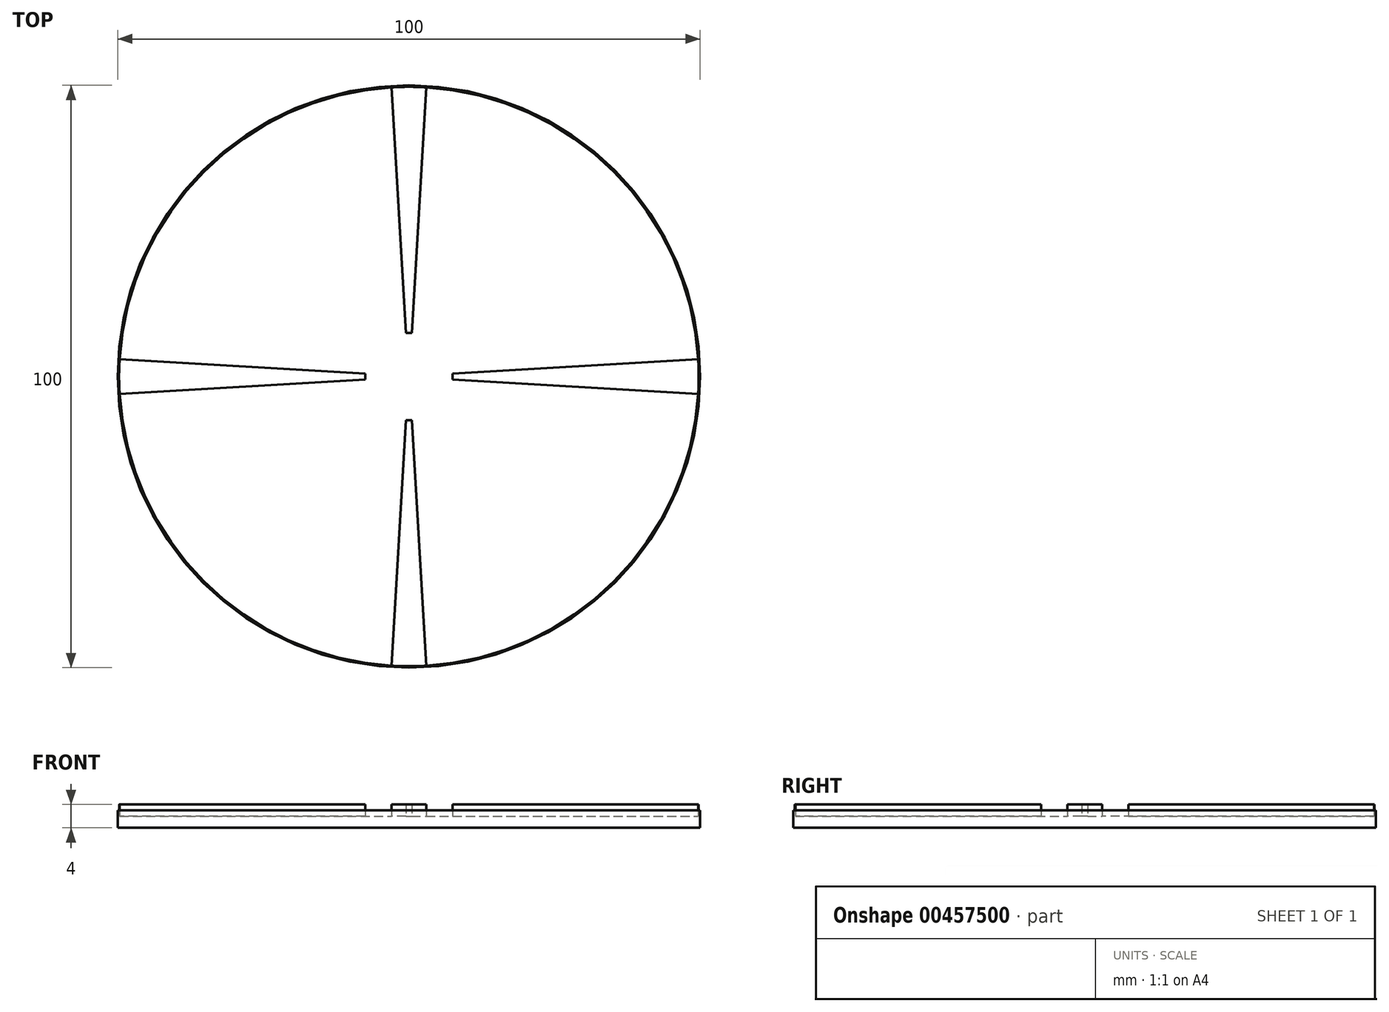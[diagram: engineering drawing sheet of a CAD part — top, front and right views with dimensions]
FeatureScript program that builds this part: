
annotation { "Feature Type Name" : "Feature", "Feature Type Description" : "" }
export const myFeature = defineFeature(function(context is Context, id is Id, definition is map)
    precondition{}
    {
        {
            var Q0;
            Q0=qCreatedBy(makeId("Top.planeOp"),FACE);
            var sketch = newSketch(context, id + "F0", { "sketchPlane" : qUnion([Q0])});
            skLineSegment(sketch, "E0.bottom", {"start": v(75, 70) * mm, "end": v(-75, 70) * mm});
            skLineSegment(sketch, "E0.top", {"start": v(75, -70) * mm, "end": v(-75, -70) * mm});
            skLineSegment(sketch, "E0.left", {"start": v(75, 70) * mm, "end": v(75, -70) * mm});
            skLineSegment(sketch, "E0.right", {"start": v(-75, 70) * mm, "end": v(-75, -70) * mm});
            skPoint(sketch, "E0.middle", {"position": v(0, 0) * mm});
            skSolve(sketch);
        }
        {
            var Q0;
            Q0=qSketchRegion(id+"F0",true);
            extrude(context, id + "F1", {"entities" : qUnion([Q0]), "depth" : 2 * mm});
        }
        {
            var Q0;
            Q0=makeQuery(id+"F1.opExtrude","CAP_FACE",FACE,{"disambiguationData":[OSD([sQuery(id+"F0.wireOp",EDGE,"E0.bottom"),sQuery(id+"F0.wireOp",EDGE,"E0.top"),sQuery(id+"F0.wireOp",EDGE,"E0.left"),sQuery(id+"F0.wireOp",EDGE,"E0.right")])],"isStart":false});
            var sketch = newSketch(context, id + "F2", { "sketchPlane" : qUnion([Q0])});
            skArc(sketch, "E1", {"start": v(-67.18, 7) * mm, "mid": v(-67.92, 8.77) * mm, "end": v(-69.68, 9.5) * mm});
            skArc(sketch, "E2.MirrorC", {"start": v(-67.18, -7) * mm, "mid": v(-67.92, -8.77) * mm, "end": v(-69.68, -9.5) * mm});
            skCircle(sketch, "E3", {"center": v(-64, 57.6) * mm, "radius": 2.5 * mm});
            skCircle(sketch, "E4.MirrorC", {"center": v(-64, -57.6) * mm, "radius": 2.5 * mm});
            skLineSegment(sketch, "E5", {"start": v(-46.5, 70) * mm, "end": v(-75, 41.5) * mm});
            skLineSegment(sketch, "E6.MirrorCS", {"start": v(-46.5, -70) * mm, "end": v(-75, -41.5) * mm});
            skLineSegment(sketch, "E7", {"start": v(-69.68, 9.5) * mm, "end": v(-75, 9.5) * mm});
            skLineSegment(sketch, "E8", {"start": v(-67.18, -7) * mm, "end": v(-67.18, 7) * mm});
            skLineSegment(sketch, "E9.MirrorCS", {"start": v(-69.68, -9.5) * mm, "end": v(-75, -9.5) * mm});
            skLineSegment(sketch, "E10", {"start": v(-15, -70) * mm, "end": v(-16.5, -66.52) * mm});
            skArc(sketch, "E11", {"start": v(-16.5, -66.52) * mm, "mid": v(-21.54, -63.23) * mm, "end": v(-26.53, -66.6) * mm});
            skLineSegment(sketch, "E12", {"start": v(-26.53, -66.6) * mm, "end": v(-27.94, -70) * mm});
            skLineSegment(sketch, "E13", {"start": v(-27.95, 70) * mm, "end": v(-26.64, 66.44) * mm});
            skLineSegment(sketch, "E14", {"start": v(-15, 70) * mm, "end": v(-16.65, 66.59) * mm});
            skArc(sketch, "E15", {"start": v(-26.64, 66.44) * mm, "mid": v(-21.6, 63.23) * mm, "end": v(-16.65, 66.59) * mm});
            skSolve(sketch);
        }
        {
            var Q0;
            Q0 = qSketchRegion(id + "F2", true);
            var Q1;
            Q1=makeQuery(id+"F2.imprint","IMPRINT",FACE,{"disambiguationData":[TD([[makeQuery(id+"F2.imprint","IMPRINT",EDGE,{"derivedFrom":sQuery(id+"F2.wireOp",EDGE,"E3")}),-1.0]])]});
            var Q2;
            {var subQ0=sQuery(id+"F2.wireOp",EDGE,"E13");Q2=makeQuery(id+"F2.imprint","IMPRINT",FACE,{"disambiguationData":[TD([[makeQuery(id+"F2.imprint","IMPRINT",EDGE,{"derivedFrom":subQ0}),1.0]])]});}
            var Q3;
            Q3=makeQuery(id+"F2.imprint","IMPRINT",FACE,{"disambiguationData":[TD([[makeQuery(id+"F2.imprint","IMPRINT",EDGE,{"derivedFrom":sQuery(id+"F2.wireOp",EDGE,"E1")}),1.0]])]});
            var Q4;
            {var subQ0=sQuery(id+"F2.wireOp",EDGE,"E10");Q4=makeQuery(id+"F2.imprint","IMPRINT",FACE,{"disambiguationData":[TD([[makeQuery(id+"F2.imprint","IMPRINT",EDGE,{"derivedFrom":subQ0}),1.0]])]});}
            var Q5;
            Q5=makeQuery(id+"F2.imprint","IMPRINT",FACE,{"disambiguationData":[TD([[makeQuery(id+"F2.imprint","IMPRINT",EDGE,{"derivedFrom":sQuery(id+"F2.wireOp",EDGE,"E4.MirrorC")}),1.0]])]});
            extrude(context, id + "F3", {"entities" : qUnion([Q0, Q1, Q2, Q3, Q4, Q5]), "operationType" : NewBodyOperationType.REMOVE, "endBound" : BoundingType.THROUGH_ALL, "oppositeDirection" : true, "depth" : 5 * mm, "offsetDistance" : 25 * mm});
        }
        {
            var Q0;
            Q0=makeQuery(id+"F1.opExtrude","CAP_FACE",FACE,{"disambiguationData":[OSD([sQuery(id+"F0.wireOp",EDGE,"E0.bottom"),sQuery(id+"F0.wireOp",EDGE,"E0.top"),sQuery(id+"F0.wireOp",EDGE,"E0.left"),sQuery(id+"F0.wireOp",EDGE,"E0.right")])],"isStart":false});
            var sketch = newSketch(context, id + "F4", { "sketchPlane" : qUnion([Q0])});
            skCircle(sketch, "E16", {"center": v(-3.16, 0) * mm, "radius": 49.75 * mm});
            skCircle(sketch, "E17", {"center": v(-3.16, 0) * mm, "radius": 50 * mm});
            skSolve(sketch);
        }
        {
            var Q0;
            Q0=makeQuery(id+"F4.imprint","IMPRINT",FACE,{"disambiguationData":[TD([[makeQuery(id+"F4.imprint","IMPRINT",EDGE,{"derivedFrom":sQuery(id+"F4.wireOp",EDGE,"E16")}),-1.0]])]});
            extrude(context, id + "F5", {"entities" : qUnion([Q0]), "operationType" : NewBodyOperationType.ADD, "depth" : 1 * mm});
        }
        {
            var Q0;
            Q0=makeQuery(id+"F5.boolean.opBoolean","SPLIT",FACE,{"disambiguationData":[TD([makeQuery(id+"F5.opExtrude","SWEPT_FACE",FACE,{"disambiguationData":[OSD([sQuery(id+"F4.wireOp",EDGE,"E16")])]})])],"derivedFrom":makeQuery(id+"F1.opExtrude","CAP_FACE",FACE,{"disambiguationData":[OSD([sQuery(id+"F0.wireOp",EDGE,"E0.bottom"),sQuery(id+"F0.wireOp",EDGE,"E0.top"),sQuery(id+"F0.wireOp",EDGE,"E0.left"),sQuery(id+"F0.wireOp",EDGE,"E0.right")])],"isStart":false})});
            var sketch = newSketch(context, id + "F6", { "sketchPlane" : qUnion([Q0])});
            skLineSegment(sketch, "E18", {"start": v(-52.91, 0) * mm, "end": v(46.59, 0) * mm});
            skLineSegment(sketch, "E19", {"start": v(-3.16, -49.75) * mm, "end": v(-3.16, 49.75) * mm});
            skPoint(sketch, "E20.center", {"position": v(-3.16, 0) * mm});
            skPoint(sketch, "E21", {"position": v(-3.16, 7.5) * mm});
            skPoint(sketch, "E22.1.0", {"position": v(-10.66, 0) * mm});
            skPoint(sketch, "E22.2.0", {"position": v(-3.16, -7.5) * mm});
            skPoint(sketch, "E22.3.0", {"position": v(4.34, 0) * mm});
            skLineSegment(sketch, "E23", {"start": v(-3.16, 7.5) * mm, "end": v(-3.66, 7.5) * mm});
            skLineSegment(sketch, "E24", {"start": v(-3.66, 7.5) * mm, "end": v(-6.16, 49.66) * mm});
            skLineSegment(sketch, "E25.MirrorCS", {"start": v(-2.66, 7.5) * mm, "end": v(-0.16, 49.66) * mm});
            skLineSegment(sketch, "E26.MirrorCS", {"start": v(-3.16, 7.5) * mm, "end": v(-2.66, 7.5) * mm});
            skLineSegment(sketch, "E27.1.0", {"start": v(-10.66, -0.5) * mm, "end": v(-52.82, -3) * mm});
            skLineSegment(sketch, "E27.1.1", {"start": v(-10.66, 0.5) * mm, "end": v(-52.82, 3) * mm});
            skLineSegment(sketch, "E27.1.2", {"start": v(-10.66, 0) * mm, "end": v(-10.66, 0.5) * mm});
            skLineSegment(sketch, "E27.1.3", {"start": v(-10.66, 0) * mm, "end": v(-10.66, -0.5) * mm});
            skLineSegment(sketch, "E27.2.0", {"start": v(-2.66, -7.5) * mm, "end": v(-0.16, -49.66) * mm});
            skLineSegment(sketch, "E27.2.1", {"start": v(-3.66, -7.5) * mm, "end": v(-6.16, -49.66) * mm});
            skLineSegment(sketch, "E27.2.2", {"start": v(-3.16, -7.5) * mm, "end": v(-3.66, -7.5) * mm});
            skLineSegment(sketch, "E27.2.3", {"start": v(-3.16, -7.5) * mm, "end": v(-2.66, -7.5) * mm});
            skLineSegment(sketch, "E27.3.0", {"start": v(4.34, 0.5) * mm, "end": v(46.5, 3) * mm});
            skLineSegment(sketch, "E27.3.1", {"start": v(4.34, -0.5) * mm, "end": v(46.5, -3) * mm});
            skLineSegment(sketch, "E27.3.2", {"start": v(4.34, 0) * mm, "end": v(4.34, -0.5) * mm});
            skLineSegment(sketch, "E27.3.3", {"start": v(4.34, 0) * mm, "end": v(4.34, 0.5) * mm});
            skSolve(sketch);
        }
        {
            var Q0;
            {var subQ4=sQuery(id+"F6.wireOp",EDGE,"E25.MirrorCS");Q0=makeQuery(id+"F6.imprint","IMPRINT",FACE,{"disambiguationData":[TD([[makeQuery(id+"F6.imprint","IMPRINT",EDGE,{"derivedFrom":subQ4}),1.0]])]});}
            var Q1;
            Q1=makeQuery(id+"F6.imprint","IMPRINT",FACE,{"disambiguationData":[TD([[makeQuery(id+"F6.imprint","IMPRINT",EDGE,{"derivedFrom":sQuery(id+"F6.wireOp",EDGE,"NAewh5kq-L7EF-FmbW-yRkp-duXd5l4xCfDB")}),-1.0]])]});
            var Q2;
            Q2=makeQuery(id+"F6.imprint","IMPRINT",FACE,{"disambiguationData":[TD([[makeQuery(id+"F6.imprint","IMPRINT",EDGE,{"derivedFrom":sQuery(id+"F6.wireOp",EDGE,"c465f5bf-b5a5-4b0b-8659-c38a877ec2590.MirrorC")}),1.0]])]});
            var Q3;
            {var subQ4=sQuery(id+"F6.wireOp",EDGE,"E27.3.1");Q3=makeQuery(id+"F6.imprint","IMPRINT",FACE,{"disambiguationData":[TD([[makeQuery(id+"F6.imprint","IMPRINT",EDGE,{"derivedFrom":subQ4}),1.0]])]});}
            var Q4;
            Q4=makeQuery(id+"F6.imprint","IMPRINT",FACE,{"disambiguationData":[TD([[makeQuery(id+"F6.imprint","IMPRINT",EDGE,{"derivedFrom":sQuery(id+"F6.wireOp",EDGE,"E20.3.0")}),1.0]])]});
            var Q5;
            Q5=makeQuery(id+"F6.imprint","IMPRINT",FACE,{"disambiguationData":[TD([[makeQuery(id+"F6.imprint","IMPRINT",EDGE,{"derivedFrom":sQuery(id+"F6.wireOp",EDGE,"E20.1.0")}),1.0]])]});
            var Q6;
            {var subQ4=sQuery(id+"F6.wireOp",EDGE,"E27.1.1");Q6=makeQuery(id+"F6.imprint","IMPRINT",FACE,{"disambiguationData":[TD([[makeQuery(id+"F6.imprint","IMPRINT",EDGE,{"derivedFrom":subQ4}),1.0]])]});}
            var Q7;
            {var subQ4=sQuery(id+"F6.wireOp",EDGE,"E27.2.1");Q7=makeQuery(id+"F6.imprint","IMPRINT",FACE,{"disambiguationData":[TD([[makeQuery(id+"F6.imprint","IMPRINT",EDGE,{"derivedFrom":subQ4}),1.0]])]});}
            var Q8;
            Q8=makeQuery(id+"F6.imprint","IMPRINT",FACE,{"disambiguationData":[TD([[makeQuery(id+"F6.imprint","IMPRINT",EDGE,{"derivedFrom":sQuery(id+"F6.wireOp",EDGE,"E20.2.0")}),1.0]])]});
            var Q9;
            {var subQ4=sQuery(id+"F6.wireOp",EDGE,"E27.3.0");Q9=makeQuery(id+"F6.imprint","IMPRINT",FACE,{"disambiguationData":[TD([[makeQuery(id+"F6.imprint","IMPRINT",EDGE,{"derivedFrom":subQ4}),-1.0]])]});}
            var Q10;
            Q10=makeQuery(id+"F6.imprint","IMPRINT",FACE,{"disambiguationData":[TD([[makeQuery(id+"F6.imprint","IMPRINT",EDGE,{"derivedFrom":sQuery(id+"F6.wireOp",EDGE,"E20.3.1")}),-1.0]])]});
            var Q11;
            Q11=makeQuery(id+"F6.imprint","IMPRINT",FACE,{"disambiguationData":[TD([[makeQuery(id+"F6.imprint","IMPRINT",EDGE,{"derivedFrom":sQuery(id+"F6.wireOp",EDGE,"E20.1.1")}),-1.0]])]});
            var Q12;
            {var subQ4=sQuery(id+"F6.wireOp",EDGE,"E27.1.0");Q12=makeQuery(id+"F6.imprint","IMPRINT",FACE,{"disambiguationData":[TD([[makeQuery(id+"F6.imprint","IMPRINT",EDGE,{"derivedFrom":subQ4}),-1.0]])]});}
            var Q13;
            Q13=makeQuery(id+"F6.imprint","IMPRINT",FACE,{"disambiguationData":[TD([[makeQuery(id+"F6.imprint","IMPRINT",EDGE,{"derivedFrom":sQuery(id+"F6.wireOp",EDGE,"E20.2.1")}),-1.0]])]});
            var Q14;
            {var subQ4=sQuery(id+"F6.wireOp",EDGE,"E27.2.0");Q14=makeQuery(id+"F6.imprint","IMPRINT",FACE,{"disambiguationData":[TD([[makeQuery(id+"F6.imprint","IMPRINT",EDGE,{"derivedFrom":subQ4}),-1.0]])]});}
            var Q15;
            {var subQ0=sQuery(id+"F6.wireOp",EDGE,"E23");Q15=makeQuery(id+"F6.imprint","IMPRINT",FACE,{"disambiguationData":[TD([[makeQuery(id+"F6.imprint","IMPRINT",EDGE,{"derivedFrom":subQ0}),-1.0]])]});}
            extrude(context, id + "F7", {"entities" : qUnion([Q0, Q1, Q2, Q3, Q4, Q5, Q6, Q7, Q8, Q9, Q10, Q11, Q12, Q13, Q14, Q15]), "operationType" : NewBodyOperationType.ADD, "depth" : 2 * mm});
        }
        {
            var Q0;
            Q0 = qSketchRegion(id + "F2", true);
            var Q1;
            {var subQ0=sQuery(id+"F2.wireOp",EDGE,"E13");Q1=makeQuery(id+"F2.imprint","IMPRINT",FACE,{"disambiguationData":[TD([[makeQuery(id+"F2.imprint","IMPRINT",EDGE,{"derivedFrom":subQ0}),1.0]])]});}
            var Q2;
            {var subQ0=sQuery(id+"F2.wireOp",EDGE,"E10");Q2=makeQuery(id+"F2.imprint","IMPRINT",FACE,{"disambiguationData":[TD([[makeQuery(id+"F2.imprint","IMPRINT",EDGE,{"derivedFrom":subQ0}),1.0]])]});}
            extrude(context, id + "F8", {"entities" : qUnion([Q0, Q1, Q2]), "operationType" : NewBodyOperationType.REMOVE, "oppositeDirection" : true, "depth" : 25 * mm, "offsetDistance" : 25 * mm});
        }
        {
            var Q0;
            Q0 = qSketchRegion(id + "F2", true);
            var Q1;
            {var subQ0=sQuery(id+"F2.wireOp",EDGE,"E13");Q1=makeQuery(id+"F2.imprint","IMPRINT",FACE,{"disambiguationData":[TD([[makeQuery(id+"F2.imprint","IMPRINT",EDGE,{"derivedFrom":subQ0}),1.0]])]});}
            var Q2;
            Q2=makeQuery(id+"F4.imprint","IMPRINT",FACE,{"disambiguationData":[TD([[makeQuery(id+"F4.imprint","IMPRINT",EDGE,{"derivedFrom":sQuery(id+"F4.wireOp",EDGE,"E17")}),-1.0]])]});
            extrude(context, id + "F9", {"entities" : qUnion([Q0, Q1, Q2]), "operationType" : NewBodyOperationType.REMOVE, "endBound" : BoundingType.THROUGH_ALL, "oppositeDirection" : true, "depth" : 25 * mm, "offsetDistance" : 25 * mm});
        }
        {
            var Q0;
            Q0=makeQuery(id+"F2.imprint","IMPRINT",FACE,{"disambiguationData":[TD([[makeQuery(id+"F2.imprint","IMPRINT",EDGE,{"derivedFrom":sQuery(id+"F2.wireOp",EDGE,"E4.MirrorC")}),1.0]])]});
            var Q1;
            Q1=makeQuery(id+"F2.imprint","IMPRINT",FACE,{"disambiguationData":[TD([[makeQuery(id+"F2.imprint","IMPRINT",EDGE,{"derivedFrom":sQuery(id+"F2.wireOp",EDGE,"E3")}),-1.0]])]});
            var Q2;
            Q2=makeQuery(id+"F2.imprint","IMPRINT",FACE,{"disambiguationData":[TD([[makeQuery(id+"F2.imprint","IMPRINT",EDGE,{"derivedFrom":sQuery(id+"F2.wireOp",EDGE,"E1")}),1.0]])]});
            var Q3;
            Q3=makeQuery(id+"F0.imprint","IMPRINT",FACE,{"disambiguationData":[TD([[makeQuery(id+"F0.imprint","IMPRINT",EDGE,{"derivedFrom":sQuery(id+"F0.wireOp",EDGE,"E0.bottom")}),1.0]])]});
            var Q4;
            {var subQ0=sQuery(id+"F2.wireOp",EDGE,"E10");Q4=makeQuery(id+"F2.imprint","IMPRINT",FACE,{"disambiguationData":[TD([[makeQuery(id+"F2.imprint","IMPRINT",EDGE,{"derivedFrom":subQ0}),1.0]])]});}
            var Q5;
            {var subQ0=sQuery(id+"F2.wireOp",EDGE,"E13");Q5=makeQuery(id+"F2.imprint","IMPRINT",FACE,{"disambiguationData":[TD([[makeQuery(id+"F2.imprint","IMPRINT",EDGE,{"derivedFrom":subQ0}),1.0]])]});}
            extrude(context, id + "F10", {"entities" : qUnion([Q0, Q1, Q2, Q3, Q4, Q5]), "operationType" : NewBodyOperationType.REMOVE, "oppositeDirection" : true, "depth" : 25 * mm, "offsetDistance" : 25 * mm});
        }
    });
